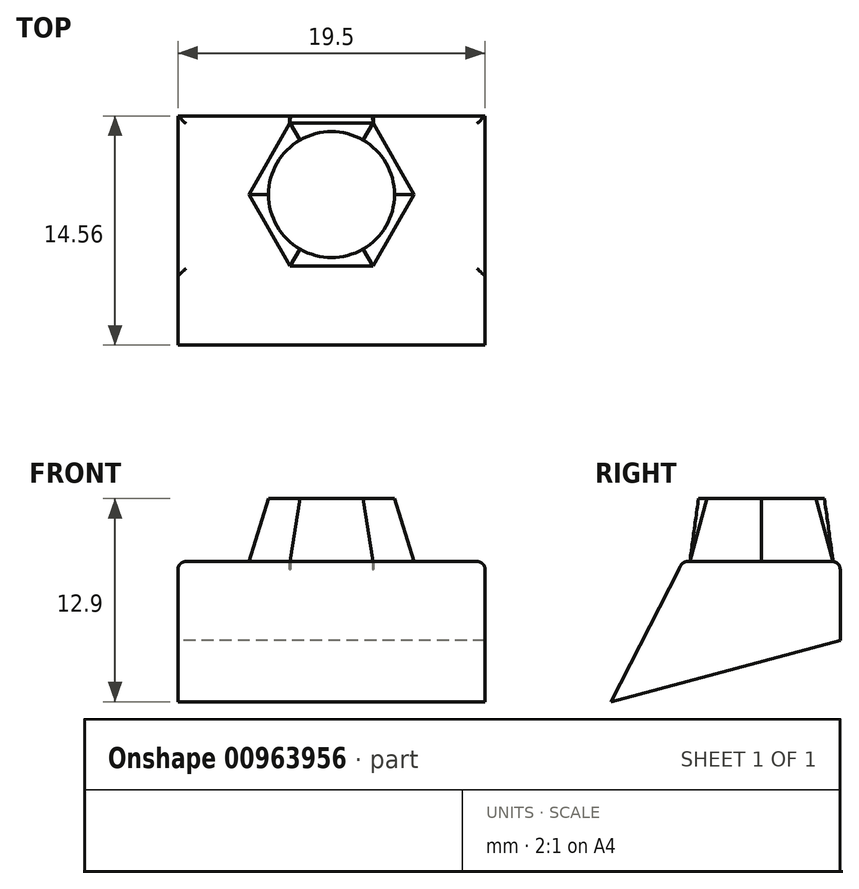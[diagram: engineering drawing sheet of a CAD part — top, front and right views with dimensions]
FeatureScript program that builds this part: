
annotation { "Feature Type Name" : "Feature", "Feature Type Description" : "" }
export const myFeature = defineFeature(function(context is Context, id is Id, definition is map)
    precondition{}
    {
        {
            var Q0;
            Q0=qCreatedBy(makeId("Right.planeOp"),FACE);
            var sketch = newSketch(context, id + "F0", { "sketchPlane" : qUnion([Q0])});
            skLineSegment(sketch, "E0", {"start": v(0, 0) * mm, "end": v(4.56, 8.9) * mm});
            skLineSegment(sketch, "E1", {"start": v(4.56, 8.9) * mm, "end": v(14.56, 8.9) * mm});
            skLineSegment(sketch, "E2", {"start": v(14.56, 8.9) * mm, "end": v(14.56, 3.9) * mm});
            skLineSegment(sketch, "E3", {"start": v(14.56, 3.9) * mm, "end": v(0, 0) * mm});
            skSolve(sketch);
        }
        {
            var Q0;
            Q0 = qSketchRegion(id + "F0", true);
            extrude(context, id + "F1", {"entities" : qUnion([Q0]), "endBound" : BoundingType.SYMMETRIC, "depth" : 19.5 * mm, "offsetDistance" : 25 * mm});
        }
        {
            var Q0;
            Q0=makeQuery(id+"F1.opExtrude","SWEPT_FACE",FACE,{"disambiguationData":[OSD([sQuery(id+"F0.wireOp",EDGE,"E1")])]});
            var sketch = newSketch(context, id + "F2", { "sketchPlane" : qUnion([Q0])});
            skCircle(sketch, "E4.cCircle", {"center": v(0, 9.56) * mm, "radius": 5.25 * mm, "construction": true});
            skLineSegment(sketch, "E4.0", {"start": v(-2.62, 14.1) * mm, "end": v(2.63, 14.1) * mm});
            skLineSegment(sketch, "E4.1", {"start": v(2.62, 14.1) * mm, "end": v(5.25, 9.56) * mm});
            skLineSegment(sketch, "E4.2", {"start": v(5.25, 9.56) * mm, "end": v(2.62, 5.01) * mm});
            skLineSegment(sketch, "E4.3", {"start": v(2.62, 5.01) * mm, "end": v(-2.62, 5.01) * mm});
            skLineSegment(sketch, "E4.4", {"start": v(-2.63, 5.01) * mm, "end": v(-5.25, 9.56) * mm});
            skLineSegment(sketch, "E4.5", {"start": v(-5.25, 9.56) * mm, "end": v(-2.62, 14.1) * mm});
            skSolve(sketch);
        }
        {
            var Q0;
            Q0=makeQuery(id+"F2.imprint","IMPRINT",FACE,{"disambiguationData":[TD([[makeQuery(id+"F2.imprint","IMPRINT",EDGE,{"derivedFrom":sQuery(id+"F2.wireOp",EDGE,"E4.0")}),1.0]])]});
            cPlane(context, id + "F3", {"entities" : qUnion([Q0]), "cplaneType" : CPlaneType.OFFSET, "offset" : 4 * mm, "width" : 150 * mm, "height" : 150 * mm});
        }
        {
            var Q0;
            Q0=qCreatedBy(id+"F3.planeOp",FACE);
            var sketch = newSketch(context, id + "F4", { "sketchPlane" : qUnion([Q0])});
            skCircle(sketch, "E5", {"center": v(0, 9.56) * mm, "radius": 4 * mm});
            skSolve(sketch);
        }
        {
            var Q1;
            Q1 = qSketchRegion(id + "F2", true);
            var Q2;
            Q2 = qSketchRegion(id + "F4", true);
            loft(context, id + "F5", {"operationType" : NewBodyOperationType.ADD, "sheetProfilesArray" : [{ "sheetProfileEntities" : qUnion([Q1]) }, { "sheetProfileEntities" : qUnion([Q2]) }]});
        }
        {
            var Q0;
            Q0=makeQuery(id+"F1.opExtrude","CAP_EDGE",EDGE,{"disambiguationData":[OSD([sQuery(id+"F0.wireOp",EDGE,"E1")])],"isStart":true});
            var Q1;
            Q1=makeQuery(id+"F1.opExtrude","SWEPT_EDGE",EDGE,{"disambiguationData":[OSD([sQuery(id+"F0.wireOp",EDGE,"E0"),sQuery(id+"F0.wireOp",EDGE,"E1")])]});
            var Q2;
            Q2=makeQuery(id+"F1.opExtrude","CAP_EDGE",EDGE,{"disambiguationData":[OSD([sQuery(id+"F0.wireOp",EDGE,"E1")])],"isStart":false});
            var Q3;
            Q3=makeQuery(id+"F1.opExtrude","SWEPT_EDGE",EDGE,{"disambiguationData":[OSD([sQuery(id+"F0.wireOp",EDGE,"E1"),sQuery(id+"F0.wireOp",EDGE,"E2")])]});
            fillet(context, id + "F6", {"entities" : qUnion([Q0, Q1, Q2, Q3]), "radius" : .5 * mm, "tangentPropagation" : true, "allowEdgeOverflow" : false});
        }
    });
